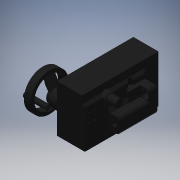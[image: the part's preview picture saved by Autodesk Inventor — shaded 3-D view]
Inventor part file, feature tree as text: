
AUTODESK INVENTOR PART (.ipt)
format: ipt  version: 2016 (Build 200138000, 138)  size: 585,216 bytes
history: native  units: in
note: dims shown in document units (in); Inventor stores cm internally (conversion verified against a paired STEP export)
features: sketch x21, extrude x17, fillet x6, reference x4, plane x3, loft x2, projected_geometry x2, chamfer x1, other x1
ambient origin geometry x8: Origin, YZ Plane, XZ Plane, XY Plane, X Axis, Y Axis, Z Axis, Center Point
bodies: Solid1 (feature_tree)
feature tree (57):
  extrude  "Extrusion1"  Depth=4.3701in
  extrude  "Extrusion2"  Depth=1.1811in
  extrude  "Extrusion3"  Depth=12.0079in TaperAngle=0.0deg
  extrude  "Extrusion4"  Depth=12.0079in TaperAngle=0.0deg
  extrude  "Extrusion5"  Depth=1.9685in
  extrude  "Extrusion6"  Depth=1.4567in TaperAngle=0.0deg
  extrude  "Extrusion7"  Depth=4.6457in TaperAngle=0.0deg
  fillet  "Fillet2"  Radius=1.7717in
  chamfer  "Chamfer1"  Distance=0.5512in
  fillet  "Fillet3"  Radius=0.7874in
  extrude  "Extrusion8"  Depth=0.5118in TaperAngle=0.0deg
  extrude  "Extrusion9"  Depth=0.315in
  extrude  "Extrusion10"  Depth=0.2559in TaperAngle=0.0deg
  fillet  "Fillet4"  Radius=0.5906in
  extrude  "Extrusion11"  Depth=0.0787in
  extrude  "Extrusion12"  Depth=0.0787in
  sketch  "Sketch14"  dims[d39=0.9449in d40=0.7874in]
  plane  "Work Plane2"
  loft  "Loft1"
  plane  "Work Plane3"
  extrude  "Extrusion13"  Depth=1.1417in
  extrude  "Extrusion15"  Depth=1.7717in
  plane  "Work Plane5"
  sketch  "Sketch22"  dims[d55=3.3071in d56=1.1811in]
  sketch  "Sketch16"  dims[d43=0.2559in d44=0.0in d45=1.7717in]
  loft  "Loft2"
  fillet  "Fillet5"  Radius=0.8268in
  extrude  "Extrusion16"  Depth=0.1181in TaperAngle=0.0deg
  fillet  "Fillet6"  Radius=0.1181in
  fillet  "Fillet7"  Radius=2.7559in
  extrude  "Extrusion17"  Depth=1.1811in
  extrude  "Extrusion18"  Depth=2.2047in
  sketch  "Sketch1"  dims[d0=3.937in d1=4.3701in]
  sketch  "Sketch2"  dims[d2=7.4803in d3=1.1811in]
  sketch  "Sketch3"  dims[d4=5.9843in d5=12.0079in d6=0.0in]
  sketch  "Sketch4"  dims[d7=2.3228in d8=12.0079in d9=0.0in]
  sketch  "Sketch5"  dims[d10=0.7087in d11=1.9685in]
  sketch  "Sketch6"  dims[d12=3.8976in d13=1.4567in d14=0.0in]
  sketch  "Sketch7"  dims[d15=1.5748in d16=4.6457in d17=0.0in d18=1.7717in d19=0.5512in d20=0.0in d21=0.7874in]
  sketch  "Sketch9"  dims[d22=0.7874in d23=0.5118in d24=0.0in]
  sketch  "Sketch10"  dims[d25=2.3622in d26=0.315in]
  sketch  "Sketch11"  dims[d27=0.5906in d28=0.2559in d29=0.0in d31=0.5906in]
  sketch  "Sketch12"  dims[d32=0.5118in d33=0.0787in d34=45.0deg d36=1.1811in]
  sketch  "Sketch13"  dims[d37=1.6142in d38=0.0787in]
  projected_geometry  "Projected Loop1"
  sketch  "Sketch15"  dims[d41=0.9646in d42=1.1417in]
  other  "Edges1"
  sketch  "Sketch18"  dims[d46=1.5748in d47=3.5827in d48=0.8268in d49=0.0in]
  sketch  "Sketch21"  dims[d50=1.2205in d51=1.4173in d52=0.0in d53=0.1181in d54=2.7559in]
  projected_geometry  "Projected Loop4"
  sketch  "Sketch23"  dims[d57=1.1417in d58=0.0in d59=2.2047in]
  sketch  "Sketch24"  dims[d60=0.2756in d61=0.0in]
  sketch  "Sketch25"  dims[d62=0.9449in d63=5.1181in d64=0.0in d65=90.0deg d66=0.0in d67=90.0deg d68=0.6693in d69=2.2047in d71=0.0in d72=90.0deg d75=2.2047in d76=4.7244in d78=0.7874in d79=0.5118in d80=0.2756in d81=0.0in d82=2.7559in d87=5.9843in d88=4.8031in d89=1.063in d90=0.0in d91=1.7717in d92=0.0in d93=90.0deg d94=0.5906in d95=0.7874in d96=2.2047in d97=1.063in d98=0.0in d99=0.0787in d100=0.0787in d101=2.7559in d102=0.0in d103=0.3937in d104=0.0in]
  reference  "Reference1"
  reference  "Reference2"
  reference  "Reference3"
  reference  "Reference4"
